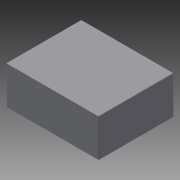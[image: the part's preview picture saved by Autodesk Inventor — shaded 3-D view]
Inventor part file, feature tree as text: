
AUTODESK INVENTOR PART (.ipt)
format: ipt  version: 2014 SP1 (Build 180222100, 222)  size: 89,600 bytes
history: native  units: in
note: dims shown in document units (in); Inventor stores cm internally (conversion verified against a paired STEP export)
features: reference x3, extrude x1, fillet x1, sketch x1
ambient origin geometry x8: Origin, YZ Plane, XZ Plane, XY Plane, X Axis, Y Axis, Z Axis, Center Point
bodies: Solid1 (feature_tree)
feature tree (6):
  extrude  "Extrusion1"  Depth=2.97in
  fillet  "Fillet1"  Radius=5.74in
  sketch  "Sketch1"  dims[d0=7.07in d1=2.97in d2=5.74in d3=0.0in d4=0.05in]
  reference  "Reference1"
  reference  "Reference2"
  reference  "Reference3"
